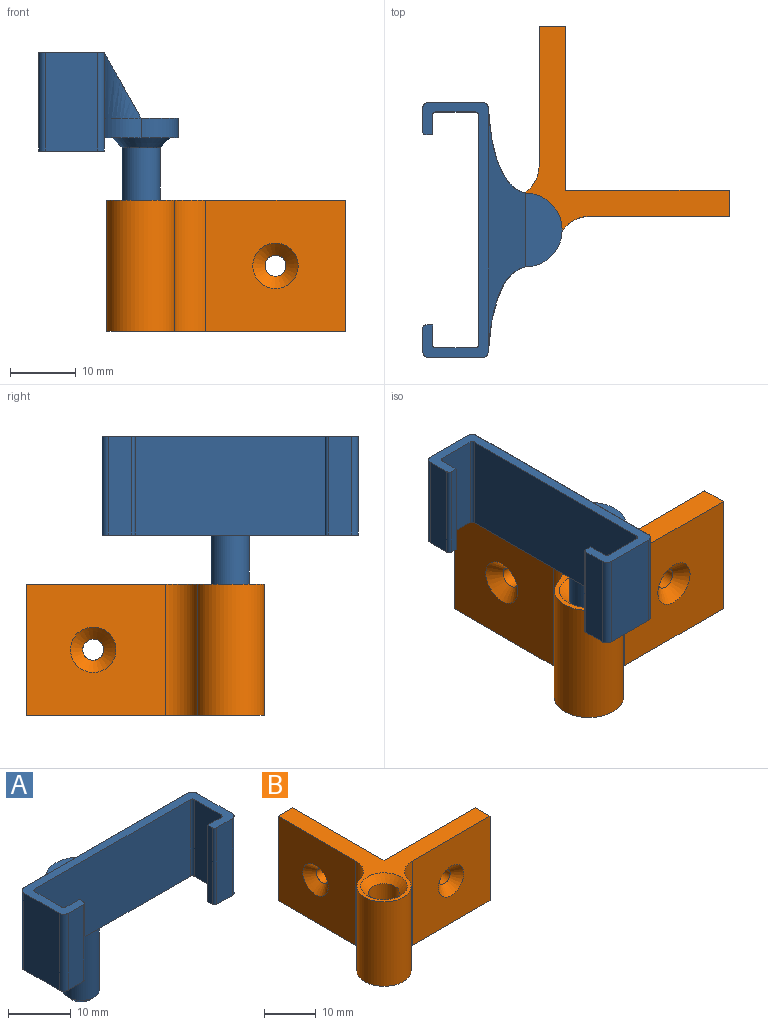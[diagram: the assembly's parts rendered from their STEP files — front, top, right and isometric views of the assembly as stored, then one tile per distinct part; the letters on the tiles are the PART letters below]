
ASSEMBLY  parts=2 mates=1
PART A: 37 faces, bbox 39x21.3x33 mm
  f0: cylinder r=5.62mm len=11.25mm, axis (0,0,-1), area 53mm2, adj f1,f2,f34,f35
  f1: plane 11.25x5.63mm, normal (0,0,1), area 49.7mm2, adj f0,f33
  f2: plane 37x11.25mm, normal (0,0,-1), area 86.6mm2, adj f0,f5,f6,f34,f35
  f3: cylinder r=2.93mm len=17.5mm, axis (0,0,-1), area 321.6mm2, adj f5,f36
  f4: plane 3.85x3.85mm, normal (0,0,-1), area 11.6mm2, adj f36
  f5: cone r=4.42mm half-angle=45deg, axis (0,0,1), area 49mm2, adj f2,f3
  f6: plane 37x2mm, normal (0,1,0), area 74mm2, adj f2,f18,f20,f30
  f7: cylinder r=0.5mm len=15mm, axis (0,0,-1), area 11.8mm2, adj f8,f28,f29,f30
  f8: plane 35x15mm, normal (0,-1,0), area 525mm2, adj f7,f9,f29,f30
  f9: cylinder r=0.5mm len=15mm, axis (0,0,-1), area 11.8mm2, adj f8,f10,f29,f30
  f10: plane 15x6mm, normal (-1,0,0), area 90mm2, adj f9,f11,f29,f30
  f11: cylinder r=0.5mm len=15mm, axis (0,0,-1), area 11.8mm2, adj f10,f12,f29,f30
  f12: plane 15x3mm, normal (0,1,0), area 45mm2, adj f11,f13,f29,f30
  f13: plane 15x1mm, normal (-1,0,0), area 15mm2, adj f12,f14,f29,f30
  f14: cylinder r=0.5mm len=15mm, axis (0,0,-1), area 11.8mm2, adj f13,f15,f29,f30
  f15: plane 15x3.5mm, normal (0,-1,0), area 52.5mm2, adj f14,f16,f29,f30
  f16: cylinder r=1mm len=15mm, axis (0,0,-1), area 23.6mm2, adj f15,f17,f29,f30
  f17: plane 15x8mm, normal (1,0,0), area 120mm2, adj f16,f18,f29,f30
  f18: cylinder r=1mm len=15mm, axis (0,0,-1), area 23.6mm2, adj f6,f17,f19,f29,f30,f32,f35
  f19: plane 37x0.06mm, normal (0,1,0), area 2.1mm2, adj f18,f20,f29,f33
  f20: cylinder r=1mm len=15mm, axis (0,0,-1), area 23.6mm2, adj f6,f19,f21,f29,f30,f31,f34
  f21: plane 15x8mm, normal (-1,0,0), area 120mm2, adj f20,f22,f29,f30
  f22: cylinder r=1mm len=15mm, axis (0,0,-1), area 23.6mm2, adj f21,f23,f29,f30
  f23: plane 15x3.5mm, normal (0,-1,0), area 52.5mm2, adj f22,f24,f29,f30
  f24: cylinder r=0.5mm len=15mm, axis (0,0,-1), area 11.8mm2, adj f23,f25,f29,f30
  f25: plane 15x1mm, normal (1,0,0), area 15mm2, adj f24,f26,f29,f30
  f26: plane 15x3mm, normal (0,1,0), area 45mm2, adj f25,f27,f29,f30
  f27: cylinder r=0.5mm len=15mm, axis (0,0,-1), area 11.8mm2, adj f26,f28,f29,f30
  f28: plane 15x6mm, normal (1,0,0), area 90mm2, adj f7,f27,f29,f30
  f29: plane 39x10mm, normal (0,0,1), area 93.7mm2, adj f7,f8,f9,f10,f11,f12,f13,f14
  f30: plane 39x10mm, normal (0,0,-1), area 93.7mm2, adj f6,f7,f8,f9,f10,f11,f12,f13
  f31: extruded ~12.88x9.94mm, area 103.5mm2, adj f20,f33,f34
  f32: extruded ~12.88x9.94mm, area 103.5mm2, adj f18,f33,f35
  f33: plane 37x9.94mm, normal (0,0.87,0.49), area 199.8mm2, adj f1,f19,f31,f32
  f34: extruded ~12.88x5.63mm, area 44.7mm2, adj f0,f2,f20,f31
  f35: extruded ~12.88x5.63mm, area 44.7mm2, adj f0,f2,f18,f32
  f36: cone r=2.93mm half-angle=45deg, axis (0,0,1), area 21.5mm2, adj f3,f4
PART B: 17 faces, bbox 36.4x36.4x20 mm
  f0: plane 21.28x20mm, normal (-1,0,0), area 387.8mm2, adj f2,f6,f7,f11,f16
  f1: plane 21.28x20mm, normal (0,-1,0), area 387.8mm2, adj f3,f6,f7,f10,f14
  f2: plane 20x4mm, normal (0,1,0), area 80mm2, adj f0,f5,f6,f7
  f3: plane 20x4mm, normal (1,0,0), area 80mm2, adj f1,f4,f6,f7
  f4: plane 25x20mm, normal (0,1,0), area 492mm2, adj f3,f5,f6,f7,f13
  f5: plane 25x20mm, normal (1,0,0), area 492mm2, adj f2,f4,f6,f7,f15
  f6: plane 36.37x36.37mm, normal (0,0,1), area 242.9mm2, adj f0,f1,f2,f3,f4,f5,f8,f10
  f7: plane 36.37x36.37mm, normal (0,0,-1), area 278.2mm2, adj f0,f1,f2,f3,f4,f5,f8,f9
  f8: cylinder r=5.25mm len=20mm, axis (0,0,-1), area 435mm2, adj f6,f7,f10,f11
  f9: cylinder r=3mm len=18.5mm, axis (0,0,-1), area 348.7mm2, adj f7,f12
  f10: cylinder r=5mm len=20mm, axis (0,0,-1), area 128.6mm2, adj f1,f6,f7,f8
  f11: cylinder r=5mm len=20mm, axis (0,0,-1), area 128.6mm2, adj f0,f6,f7,f8
  f12: cone r=3mm half-angle=45deg, axis (0,0,1), area 50mm2, adj f6,f9
  f13: cylinder r=1.6mm len=3.2mm, axis (0,-1,0), area 21.4mm2, adj f4,f14
  f14: cone r=1.6mm half-angle=45deg, axis (0,-1,0), area 42.1mm2, adj f1,f13
  f15: cylinder r=1.6mm len=3.2mm, axis (-1,0,0), area 21.4mm2, adj f5,f16
  f16: cone r=1.6mm half-angle=45deg, axis (-1,0,0), area 42.1mm2, adj f0,f15
PLACE A rot(axis=(0,0,-1),90deg) t=(10.39,55.66,9.7)mm
PLACE B t=(16.51,61.78,0.2)mm
MATE cylindrical A.f3 <-> B.f8  axis (0,0,-1) through (10.39,55.66,19.45)mm
